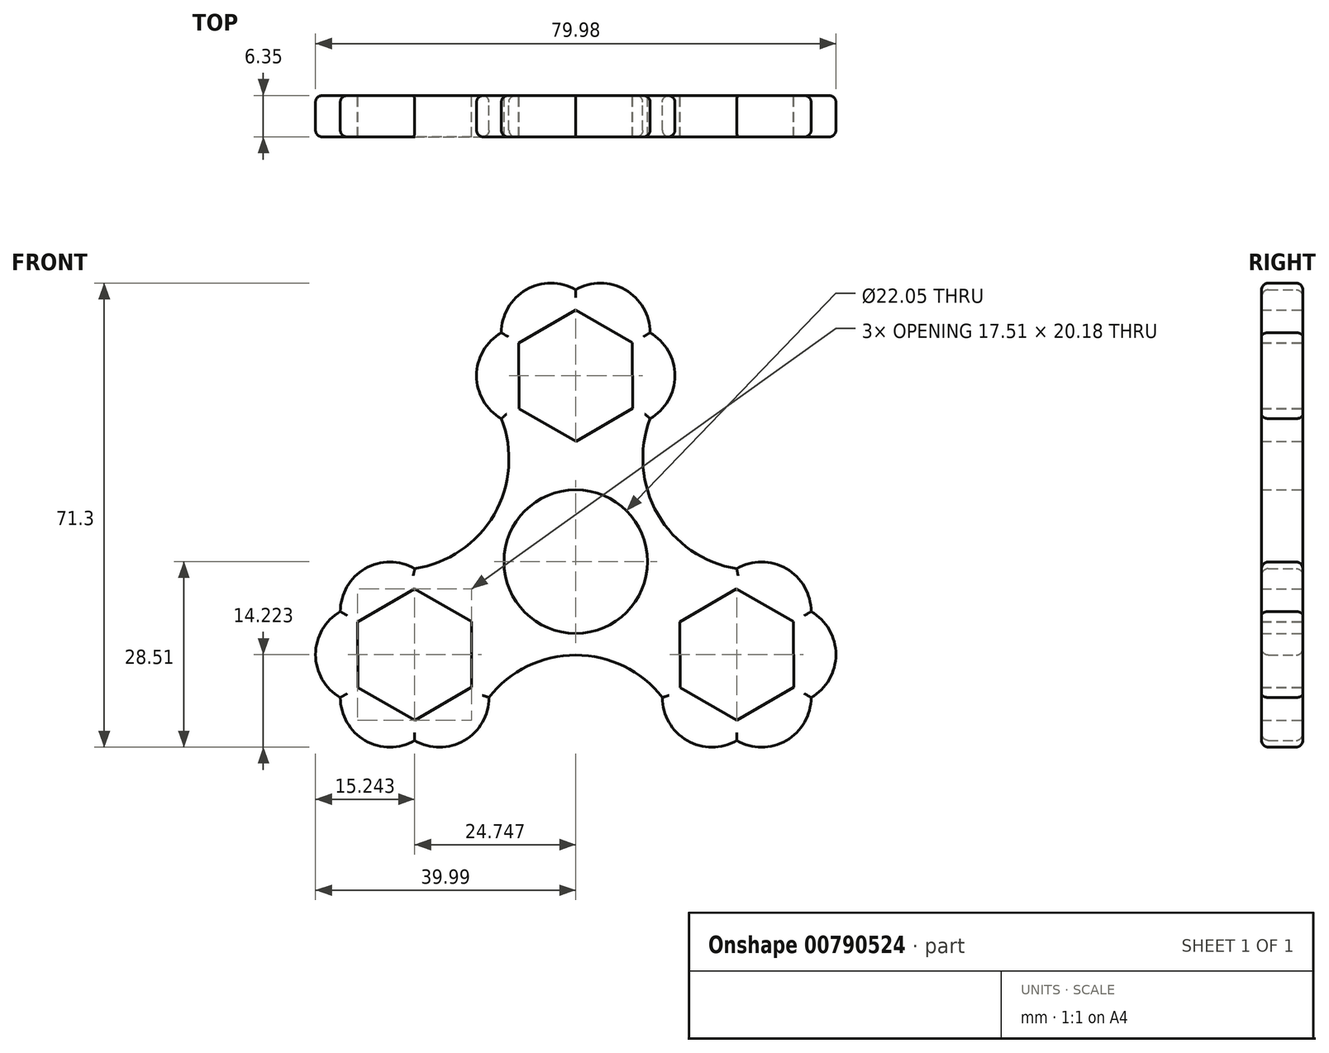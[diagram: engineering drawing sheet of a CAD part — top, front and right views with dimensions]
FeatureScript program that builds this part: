
annotation { "Feature Type Name" : "Feature", "Feature Type Description" : "" }
export const myFeature = defineFeature(function(context is Context, id is Id, definition is map)
    precondition{}
    {
        {
            var Q0;
            Q0=qCreatedBy(makeId("Front.planeOp"),FACE);
            var sketch = newSketch(context, id + "F0", { "sketchPlane" : qUnion([Q0])});
            skCircle(sketch, "E0", {"center": v(0, 0) * mm, "radius": 11.02 * mm});
            skCircle(sketch, "E1", {"center": v(0, 0) * mm, "radius": 14.29 * mm});
            skCircle(sketch, "E2.cCircle", {"center": v(0, 28.58) * mm, "radius": 11.43 * mm, "construction": true});
            skLineSegment(sketch, "E2.0", {"start": v(11.43, 35.17) * mm, "end": v(11.43, 21.98) * mm});
            skLineSegment(sketch, "E2.1", {"start": v(11.43, 21.98) * mm, "end": v(0, 15.38) * mm});
            skLineSegment(sketch, "E2.2", {"start": v(0, 15.38) * mm, "end": v(-11.43, 21.98) * mm});
            skLineSegment(sketch, "E2.3", {"start": v(-11.43, 21.98) * mm, "end": v(-11.43, 35.17) * mm});
            skLineSegment(sketch, "E2.4", {"start": v(-11.43, 35.17) * mm, "end": v(0, 41.77) * mm});
            skLineSegment(sketch, "E2.5", {"start": v(0, 41.77) * mm, "end": v(11.43, 35.17) * mm});
            skPoint(sketch, "E2.0.midPoint", {"position": v(11.43, 28.58) * mm});
            skCircle(sketch, "E3.cCircle", {"center": v(0, 28.58) * mm, "radius": 8.74 * mm, "construction": true});
            skLineSegment(sketch, "E3.0", {"start": v(8.76, 23.56) * mm, "end": v(0.04, 18.49) * mm});
            skLineSegment(sketch, "E3.1", {"start": v(0.04, 18.49) * mm, "end": v(-8.72, 23.5) * mm});
            skLineSegment(sketch, "E3.2", {"start": v(-8.72, 23.5) * mm, "end": v(-8.76, 33.59) * mm});
            skLineSegment(sketch, "E3.3", {"start": v(-8.76, 33.59) * mm, "end": v(-0.04, 38.66) * mm});
            skLineSegment(sketch, "E3.4", {"start": v(-0.04, 38.66) * mm, "end": v(8.72, 33.65) * mm});
            skLineSegment(sketch, "E3.5", {"start": v(8.72, 33.65) * mm, "end": v(8.76, 23.56) * mm});
            skPoint(sketch, "E3.0.midPoint", {"position": v(4.4, 21.02) * mm});
            skLineSegment(sketch, "E4", {"start": v(0, 28.58) * mm, "end": v(0, 0) * mm});
            skCircle(sketch, "E5.1.0", {"center": v(-24.75, -14.29) * mm, "radius": 8.74 * mm, "construction": true});
            skLineSegment(sketch, "E5.1.1", {"start": v(-24.78, -4.2) * mm, "end": v(-16.03, -9.21) * mm});
            skLineSegment(sketch, "E5.1.2", {"start": v(-33.47, -19.36) * mm, "end": v(-33.5, -9.27) * mm});
            skLineSegment(sketch, "E5.1.3", {"start": v(-36.18, -20.89) * mm, "end": v(-36.18, -7.69) * mm});
            skLineSegment(sketch, "E5.1.4", {"start": v(-24.71, -24.38) * mm, "end": v(-33.47, -19.36) * mm});
            skLineSegment(sketch, "E5.1.5", {"start": v(-16.03, -9.21) * mm, "end": v(-16, -19.3) * mm});
            skLineSegment(sketch, "E5.1.6", {"start": v(-13.32, -20.89) * mm, "end": v(-24.75, -27.49) * mm});
            skLineSegment(sketch, "E5.1.7", {"start": v(-13.32, -7.69) * mm, "end": v(-13.32, -20.89) * mm});
            skLineSegment(sketch, "E5.1.8", {"start": v(-24.75, -27.49) * mm, "end": v(-36.18, -20.89) * mm});
            skLineSegment(sketch, "E5.1.9", {"start": v(-24.75, -1.09) * mm, "end": v(-13.32, -7.69) * mm});
            skLineSegment(sketch, "E5.1.10", {"start": v(-16, -19.3) * mm, "end": v(-24.71, -24.38) * mm});
            skLineSegment(sketch, "E5.1.11", {"start": v(-36.18, -7.69) * mm, "end": v(-24.75, -1.09) * mm});
            skCircle(sketch, "E5.1.12", {"center": v(-24.75, -14.29) * mm, "radius": 11.43 * mm, "construction": true});
            skPoint(sketch, "E5.1.13", {"position": v(-30.46, -4.39) * mm});
            skPoint(sketch, "E5.1.14", {"position": v(-20.4, -6.7) * mm});
            skLineSegment(sketch, "E5.1.15", {"start": v(-33.5, -9.27) * mm, "end": v(-24.78, -4.2) * mm});
            skCircle(sketch, "E5.2.0", {"center": v(24.75, -14.29) * mm, "radius": 8.74 * mm, "construction": true});
            skLineSegment(sketch, "E5.2.1", {"start": v(16.03, -19.36) * mm, "end": v(16, -9.27) * mm});
            skLineSegment(sketch, "E5.2.2", {"start": v(33.5, -19.3) * mm, "end": v(24.78, -24.38) * mm});
            skLineSegment(sketch, "E5.2.3", {"start": v(36.18, -20.89) * mm, "end": v(24.75, -27.49) * mm});
            skLineSegment(sketch, "E5.2.4", {"start": v(33.47, -9.21) * mm, "end": v(33.5, -19.3) * mm});
            skLineSegment(sketch, "E5.2.5", {"start": v(16, -9.27) * mm, "end": v(24.71, -4.2) * mm});
            skLineSegment(sketch, "E5.2.6", {"start": v(24.75, -1.09) * mm, "end": v(36.18, -7.69) * mm});
            skLineSegment(sketch, "E5.2.7", {"start": v(13.32, -7.69) * mm, "end": v(24.75, -1.09) * mm});
            skLineSegment(sketch, "E5.2.8", {"start": v(36.18, -7.69) * mm, "end": v(36.18, -20.89) * mm});
            skLineSegment(sketch, "E5.2.9", {"start": v(13.32, -20.89) * mm, "end": v(13.32, -7.69) * mm});
            skLineSegment(sketch, "E5.2.10", {"start": v(24.71, -4.2) * mm, "end": v(33.47, -9.21) * mm});
            skLineSegment(sketch, "E5.2.11", {"start": v(24.75, -27.49) * mm, "end": v(13.32, -20.89) * mm});
            skCircle(sketch, "E5.2.12", {"center": v(24.75, -14.29) * mm, "radius": 11.43 * mm, "construction": true});
            skPoint(sketch, "E5.2.13", {"position": v(19.03, -24.19) * mm});
            skPoint(sketch, "E5.2.14", {"position": v(16, -14.32) * mm});
            skLineSegment(sketch, "E5.2.15", {"start": v(24.78, -24.38) * mm, "end": v(16.03, -19.36) * mm});
            skArc(sketch, "E6", {"start": v(13.32, -20.89) * mm, "mid": v(0, -14.37) * mm, "end": v(-13.32, -20.89) * mm});
            skArc(sketch, "E7", {"start": v(11.43, 21.98) * mm, "mid": v(12.61, 7.28) * mm, "end": v(24.75, -1.09) * mm});
            skArc(sketch, "E8", {"start": v(-11.43, 35.17) * mm, "mid": v(-15.24, 28.57) * mm, "end": v(-11.43, 21.98) * mm});
            skArc(sketch, "E9", {"start": v(0, 41.77) * mm, "mid": v(-7.62, 41.77) * mm, "end": v(-11.43, 35.17) * mm});
            skArc(sketch, "E10", {"start": v(11.43, 35.17) * mm, "mid": v(7.62, 41.77) * mm, "end": v(0, 41.77) * mm});
            skArc(sketch, "E11", {"start": v(11.43, 21.98) * mm, "mid": v(15.24, 28.58) * mm, "end": v(11.43, 35.17) * mm});
            skArc(sketch, "E12", {"start": v(-24.75, -1.09) * mm, "mid": v(-32.37, -1.09) * mm, "end": v(-36.18, -7.69) * mm});
            skArc(sketch, "E13", {"start": v(-36.18, -7.69) * mm, "mid": v(-39.99, -14.29) * mm, "end": v(-36.18, -20.89) * mm});
            skArc(sketch, "E14", {"start": v(-36.18, -20.89) * mm, "mid": v(-32.37, -27.49) * mm, "end": v(-24.75, -27.49) * mm});
            skArc(sketch, "E15", {"start": v(-24.75, -27.49) * mm, "mid": v(-17.13, -27.49) * mm, "end": v(-13.32, -20.89) * mm});
            skArc(sketch, "E16", {"start": v(13.32, -20.89) * mm, "mid": v(17.13, -27.49) * mm, "end": v(24.75, -27.49) * mm});
            skArc(sketch, "E17", {"start": v(24.75, -27.49) * mm, "mid": v(32.37, -27.49) * mm, "end": v(36.18, -20.89) * mm});
            skArc(sketch, "E18", {"start": v(36.18, -20.89) * mm, "mid": v(39.99, -14.29) * mm, "end": v(36.18, -7.69) * mm});
            skArc(sketch, "E19", {"start": v(36.18, -7.69) * mm, "mid": v(32.37, -1.09) * mm, "end": v(24.75, -1.09) * mm});
            skArc(sketch, "E20", {"start": v(-24.75, -1.09) * mm, "mid": v(-12.54, 7.24) * mm, "end": v(-11.43, 21.98) * mm});
            skSolve(sketch);
        }
        {
            var Q0;
            Q0=makeQuery(id+"F0.imprint","IMPRINT",FACE,{"disambiguationData":[TD([[makeQuery(id+"F0.imprint","IMPRINT",EDGE,{"derivedFrom":sQuery(id+"F0.wireOp",EDGE,"E2.3")}),1.0]])]});
            var Q1;
            Q1=makeQuery(id+"F0.imprint","IMPRINT",FACE,{"disambiguationData":[TD([[makeQuery(id+"F0.imprint","IMPRINT",EDGE,{"derivedFrom":sQuery(id+"F0.wireOp",EDGE,"E2.4")}),1.0]])]});
            var Q2;
            Q2=makeQuery(id+"F0.imprint","IMPRINT",FACE,{"disambiguationData":[TD([[makeQuery(id+"F0.imprint","IMPRINT",EDGE,{"derivedFrom":sQuery(id+"F0.wireOp",EDGE,"E2.5")}),1.0]])]});
            var Q3;
            Q3=makeQuery(id+"F0.imprint","IMPRINT",FACE,{"disambiguationData":[TD([[makeQuery(id+"F0.imprint","IMPRINT",EDGE,{"derivedFrom":sQuery(id+"F0.wireOp",EDGE,"E2.0")}),1.0]])]});
            var Q4;
            Q4=makeQuery(id+"F0.imprint","IMPRINT",FACE,{"disambiguationData":[TD([[makeQuery(id+"F0.imprint","IMPRINT",EDGE,{"derivedFrom":sQuery(id+"F0.wireOp",EDGE,"E5.2.6")}),1.0]])]});
            var Q5;
            Q5=makeQuery(id+"F0.imprint","IMPRINT",FACE,{"disambiguationData":[TD([[makeQuery(id+"F0.imprint","IMPRINT",EDGE,{"derivedFrom":sQuery(id+"F0.wireOp",EDGE,"E5.2.8")}),1.0]])]});
            var Q6;
            Q6=makeQuery(id+"F0.imprint","IMPRINT",FACE,{"disambiguationData":[TD([[makeQuery(id+"F0.imprint","IMPRINT",EDGE,{"derivedFrom":sQuery(id+"F0.wireOp",EDGE,"E5.2.3")}),1.0]])]});
            var Q7;
            Q7=makeQuery(id+"F0.imprint","IMPRINT",FACE,{"disambiguationData":[TD([[makeQuery(id+"F0.imprint","IMPRINT",EDGE,{"derivedFrom":sQuery(id+"F0.wireOp",EDGE,"E5.2.11")}),1.0]])]});
            var Q8;
            Q8=makeQuery(id+"F0.imprint","IMPRINT",FACE,{"disambiguationData":[TD([[makeQuery(id+"F0.imprint","IMPRINT",EDGE,{"derivedFrom":sQuery(id+"F0.wireOp",EDGE,"E0")}),-1.0]])]});
            var Q9;
            Q9=makeQuery(id+"F0.imprint","IMPRINT",FACE,{"disambiguationData":[TD([[makeQuery(id+"F0.imprint","IMPRINT",EDGE,{"derivedFrom":sQuery(id+"F0.wireOp",EDGE,"E5.1.1")}),1.0]])]});
            var Q10;
            Q10=makeQuery(id+"F0.imprint","IMPRINT",FACE,{"disambiguationData":[TD([[makeQuery(id+"F0.imprint","IMPRINT",EDGE,{"derivedFrom":sQuery(id+"F0.wireOp",EDGE,"E5.1.11")}),1.0]])]});
            var Q11;
            Q11=makeQuery(id+"F0.imprint","IMPRINT",FACE,{"disambiguationData":[TD([[makeQuery(id+"F0.imprint","IMPRINT",EDGE,{"derivedFrom":sQuery(id+"F0.wireOp",EDGE,"E5.1.3")}),1.0]])]});
            var Q12;
            Q12=makeQuery(id+"F0.imprint","IMPRINT",FACE,{"disambiguationData":[TD([[makeQuery(id+"F0.imprint","IMPRINT",EDGE,{"derivedFrom":sQuery(id+"F0.wireOp",EDGE,"E5.1.8")}),1.0]])]});
            var Q13;
            Q13=makeQuery(id+"F0.imprint","IMPRINT",FACE,{"disambiguationData":[TD([[makeQuery(id+"F0.imprint","IMPRINT",EDGE,{"derivedFrom":sQuery(id+"F0.wireOp",EDGE,"E5.1.6")}),1.0]])]});
            var Q14;
            Q14=makeQuery(id+"F0.imprint","IMPRINT",FACE,{"disambiguationData":[TD([[makeQuery(id+"F0.imprint","IMPRINT",EDGE,{"derivedFrom":sQuery(id+"F0.wireOp",EDGE,"E5.2.1")}),1.0]])]});
            var Q15;
            Q15=makeQuery(id+"F0.imprint","IMPRINT",FACE,{"disambiguationData":[TD([[makeQuery(id+"F0.imprint","IMPRINT",EDGE,{"derivedFrom":sQuery(id+"F0.wireOp",EDGE,"E2.0")}),-1.0]])]});
            var Q16;
            Q16=makeQuery(id+"F0.imprint","IMPRINT",FACE,{"disambiguationData":[TD([[makeQuery(id+"F0.imprint","IMPRINT",EDGE,{"derivedFrom":sQuery(id+"F0.wireOp",EDGE,"E1")}),-1.0]])]});
            extrude(context, id + "F1", {"entities" : qUnion([Q0, Q1, Q2, Q3, Q4, Q5, Q6, Q7, Q8, Q9, Q10, Q11, Q12, Q13, Q14, Q15, Q16]), "depth" : 6.35 * mm, "offsetDistance" : 25.4 * mm});
        }
        {
            var Q0;
            Q0=makeQuery(id+"F1.opExtrude","CAP_EDGE",EDGE,{"disambiguationData":[OSD([sQuery(id+"F0.wireOp",EDGE,"E8")])],"isStart":false});
            var Q1;
            Q1=makeQuery(id+"F1.opExtrude","CAP_EDGE",EDGE,{"disambiguationData":[OSD([sQuery(id+"F0.wireOp",EDGE,"E20")])],"isStart":false});
            fillet(context, id + "F2", {"entities" : qUnion([Q0, Q1]), "radius" : 1.02 * mm, "tangentPropagation" : true, "allowEdgeOverflow" : false});
        }
        {
            var Q0;
            Q0=makeQuery(id+"F1.opExtrude","CAP_EDGE",EDGE,{"disambiguationData":[OSD([sQuery(id+"F0.wireOp",EDGE,"E10")])],"isStart":true});
            var Q1;
            Q1=makeQuery(id+"F1.opExtrude","CAP_EDGE",EDGE,{"disambiguationData":[OSD([sQuery(id+"F0.wireOp",EDGE,"E11")])],"isStart":false});
            var Q2;
            Q2=makeQuery(id+"F1.opExtrude","CAP_EDGE",EDGE,{"disambiguationData":[OSD([sQuery(id+"F0.wireOp",EDGE,"E12")])],"isStart":false});
            var Q3;
            Q3=makeQuery(id+"F1.opExtrude","CAP_EDGE",EDGE,{"disambiguationData":[OSD([sQuery(id+"F0.wireOp",EDGE,"E13")])],"isStart":false});
            var Q4;
            Q4=makeQuery(id+"F1.opExtrude","CAP_EDGE",EDGE,{"disambiguationData":[OSD([sQuery(id+"F0.wireOp",EDGE,"E14")])],"isStart":false});
            var Q5;
            Q5=makeQuery(id+"F1.opExtrude","CAP_EDGE",EDGE,{"disambiguationData":[OSD([sQuery(id+"F0.wireOp",EDGE,"E15")])],"isStart":false});
            var Q6;
            Q6=makeQuery(id+"F1.opExtrude","CAP_EDGE",EDGE,{"disambiguationData":[OSD([sQuery(id+"F0.wireOp",EDGE,"E16")])],"isStart":false});
            var Q7;
            Q7=makeQuery(id+"F1.opExtrude","CAP_EDGE",EDGE,{"disambiguationData":[OSD([sQuery(id+"F0.wireOp",EDGE,"E17")])],"isStart":false});
            var Q8;
            Q8=makeQuery(id+"F1.opExtrude","CAP_EDGE",EDGE,{"disambiguationData":[OSD([sQuery(id+"F0.wireOp",EDGE,"E18")])],"isStart":false});
            var Q9;
            Q9=makeQuery(id+"F1.opExtrude","CAP_EDGE",EDGE,{"disambiguationData":[OSD([sQuery(id+"F0.wireOp",EDGE,"E19")])],"isStart":false});
            var Q10;
            Q10=makeQuery(id+"F1.opExtrude","CAP_EDGE",EDGE,{"disambiguationData":[OSD([sQuery(id+"F0.wireOp",EDGE,"E9")])],"isStart":true});
            var Q11;
            Q11=makeQuery(id+"F1.opExtrude","CAP_EDGE",EDGE,{"disambiguationData":[OSD([sQuery(id+"F0.wireOp",EDGE,"E8")])],"isStart":true});
            var Q12;
            Q12=makeQuery(id+"F1.opExtrude","CAP_EDGE",EDGE,{"disambiguationData":[OSD([sQuery(id+"F0.wireOp",EDGE,"E20")])],"isStart":true});
            var Q13;
            Q13=makeQuery(id+"F1.opExtrude","CAP_EDGE",EDGE,{"disambiguationData":[OSD([sQuery(id+"F0.wireOp",EDGE,"E12")])],"isStart":true});
            var Q14;
            Q14=makeQuery(id+"F1.opExtrude","CAP_EDGE",EDGE,{"disambiguationData":[OSD([sQuery(id+"F0.wireOp",EDGE,"E13")])],"isStart":true});
            var Q15;
            Q15=makeQuery(id+"F1.opExtrude","CAP_EDGE",EDGE,{"disambiguationData":[OSD([sQuery(id+"F0.wireOp",EDGE,"E14")])],"isStart":true});
            var Q16;
            Q16=makeQuery(id+"F1.opExtrude","CAP_EDGE",EDGE,{"disambiguationData":[OSD([sQuery(id+"F0.wireOp",EDGE,"E15")])],"isStart":true});
            var Q17;
            Q17=makeQuery(id+"F1.opExtrude","CAP_EDGE",EDGE,{"disambiguationData":[OSD([sQuery(id+"F0.wireOp",EDGE,"E6")])],"isStart":true});
            var Q18;
            Q18=makeQuery(id+"F1.opExtrude","CAP_EDGE",EDGE,{"disambiguationData":[OSD([sQuery(id+"F0.wireOp",EDGE,"E16")])],"isStart":true});
            var Q19;
            Q19=makeQuery(id+"F1.opExtrude","CAP_EDGE",EDGE,{"disambiguationData":[OSD([sQuery(id+"F0.wireOp",EDGE,"E17")])],"isStart":true});
            var Q20;
            Q20=makeQuery(id+"F1.opExtrude","CAP_EDGE",EDGE,{"disambiguationData":[OSD([sQuery(id+"F0.wireOp",EDGE,"E18")])],"isStart":true});
            var Q21;
            Q21=makeQuery(id+"F1.opExtrude","CAP_EDGE",EDGE,{"disambiguationData":[OSD([sQuery(id+"F0.wireOp",EDGE,"E7")])],"isStart":true});
            var Q22;
            Q22=makeQuery(id+"F1.opExtrude","CAP_EDGE",EDGE,{"disambiguationData":[OSD([sQuery(id+"F0.wireOp",EDGE,"E7")])],"isStart":false});
            var Q23;
            Q23=makeQuery(id+"F1.opExtrude","CAP_EDGE",EDGE,{"disambiguationData":[OSD([sQuery(id+"F0.wireOp",EDGE,"E19")])],"isStart":true});
            var Q24;
            Q24=makeQuery(id+"F1.opExtrude","CAP_EDGE",EDGE,{"disambiguationData":[OSD([sQuery(id+"F0.wireOp",EDGE,"E11")])],"isStart":true});
            var Q25;
            Q25=makeQuery(id+"F1.opExtrude","CAP_EDGE",EDGE,{"disambiguationData":[OSD([sQuery(id+"F0.wireOp",EDGE,"E10")])],"isStart":false});
            var Q26;
            Q26=makeQuery(id+"F1.opExtrude","CAP_EDGE",EDGE,{"disambiguationData":[OSD([sQuery(id+"F0.wireOp",EDGE,"E9")])],"isStart":false});
            var Q27;
            {var subQ0=sQuery(id+"F0.wireOp",EDGE,"E8");Q27=makeQuery(id+"F2.opFillet","BLEND_EDGE",EDGE,{"blendedFrom":[makeQuery(id+"F1.opExtrude","CAP_EDGE",EDGE,{"disambiguationData":[OSD([subQ0])],"isStart":false}),makeQuery(id+"F1.opExtrude","SWEPT_FACE",FACE,{"disambiguationData":[OSD([subQ0])]})],"blendedInto":[makeQuery(id+"F1.opExtrude","SWEPT_FACE",FACE,{"disambiguationData":[OSD([subQ0])]})]});}
            var Q28;
            Q28=makeQuery(id+"F1.opExtrude","CAP_EDGE",EDGE,{"disambiguationData":[OSD([sQuery(id+"F0.wireOp",EDGE,"E6")])],"isStart":false});
            fillet(context, id + "F3", {"entities" : qUnion([Q0, Q1, Q2, Q3, Q4, Q5, Q6, Q7, Q8, Q9, Q10, Q11, Q12, Q13, Q14, Q15, Q16, Q17, Q18, Q19, Q20, Q21, Q22, Q23, Q24, Q25, Q26, Q27, Q28]), "radius" : 1.02 * mm, "tangentPropagation" : true, "allowEdgeOverflow" : false});
        }
    });
